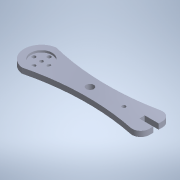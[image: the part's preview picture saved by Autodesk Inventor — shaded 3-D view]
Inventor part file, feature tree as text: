
AUTODESK INVENTOR PART (.ipt)
format: ipt  version: 2020 (Build 240168000, 168)  size: 174,080 bytes
history: mixed  units: mm
features: extrude x7, sketch x7, other x6, reference x4, fillet x1, imported_body x1
ambient origin geometry x8: Origin, YZ Plane, XZ Plane, XY Plane, X Axis, Y Axis, Z Axis, Center Point
bodies: Body1 (imported_parasolid)
feature tree (26):
  other  "Твердое тело1"
  extrude  "Выдавливание1"  Depth=10.0mm TaperAngle=0.0deg
  extrude  "Выдавливание2"  Depth=10.0mm TaperAngle=0.0deg
  extrude  "Выдавливание3"  Depth=10.0mm TaperAngle=0.0deg
  extrude  "Выдавливание4"  Depth=10.0mm TaperAngle=0.0deg
  extrude  "Выдавливание5"  Depth=10.0mm TaperAngle=0.0deg
  extrude  "Выдавливание6"  Depth=3.4mm
  extrude  "Выдавливание7"  Depth=7.1mm
  sketch  "Эскиз1"
  sketch  "Эскиз2"
  sketch  "Эскиз3"
  reference  "Ссылка2"
  sketch  "Эскиз4"
  sketch  "Эскиз5"
  reference  "Ссылка3"
  sketch  "Эскиз6"
  sketch  "Эскиз7"
  reference  "Ссылка8"
  reference  "Ссылка9"
  fillet  "Redondeo1"  Radius=40.0mm
  parser-record x1  (decoder bookkeeping rows leaked as tree rows — omitted from the tree; the rows remain in map.json)
  other  "Analisis_brazo.iam"
  other  "Ensamblaje1:1"
  other  "BASE_2.1:1"
  other  "Servo krepej:3"
  imported_body  NMx_Import_Brep_tag  [imported B-rep: ~21 faces, bbox_mm=[115.8, 5.0, 32.164254]]
note: 1 file-system path scrubbed to <path> (originals preserved in map.json)
